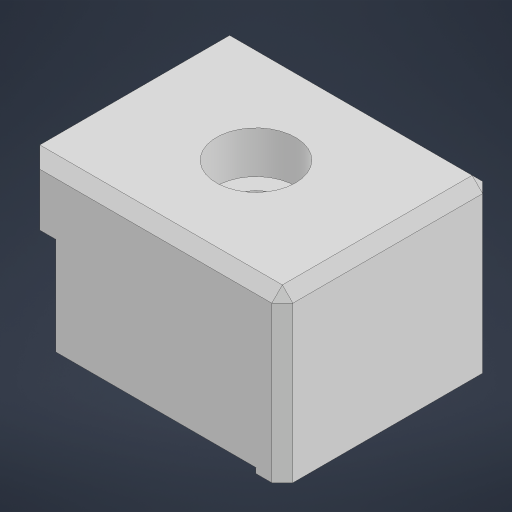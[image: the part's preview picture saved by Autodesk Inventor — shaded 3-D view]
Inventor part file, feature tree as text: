
AUTODESK INVENTOR PART (.ipt)
format: ipt  version: 2024.1 (Build 281209000, 209)  size: 183,808 bytes
history: native  units: mm
features: chamfer x2, sketch x2, extrude x1, hole x1, projected_geometry x1
ambient origin geometry x8: Origin, YZ Plane, XZ Plane, XY Plane, X Axis, Y Axis, Z Axis, Center Point
bodies: Solid1 (feature_tree)
feature tree (7):
  extrude  "Extrusion1"  Depth=31.5mm
  hole  "Hole1"  [1 undecoded]
  chamfer  "Chamfer1"  Distance=5.0mm
  chamfer  "Chamfer2"  Distance=40.0mm
  sketch  "Sketch1"  dims[d0=50.0mm d1=31.5mm]
  sketch  "Sketch2"  dims[d2=1.0mm d3=7.0mm d5=5.0mm d6=40.0mm d7=0.0mm d8=8.5mm d9=6.0mm d10=15.0mm d11=8.0mm d12=90.0deg d13=8.0mm d14=20.594885mm d15=2.0mm d16=2.0mm d17=45.0deg d18=4.0mm d19=2.0mm d20=45.0deg d23=18.0mm d24=12.0mm d25=19.5mm d26=38.0mm]
  projected_geometry  "Projected Loop1"
note: 1 required parameter value undecoded (feature->parameter linkage not recoverable at this tier; creation-order binding heuristic only, values carry confidence <= 0.55)
